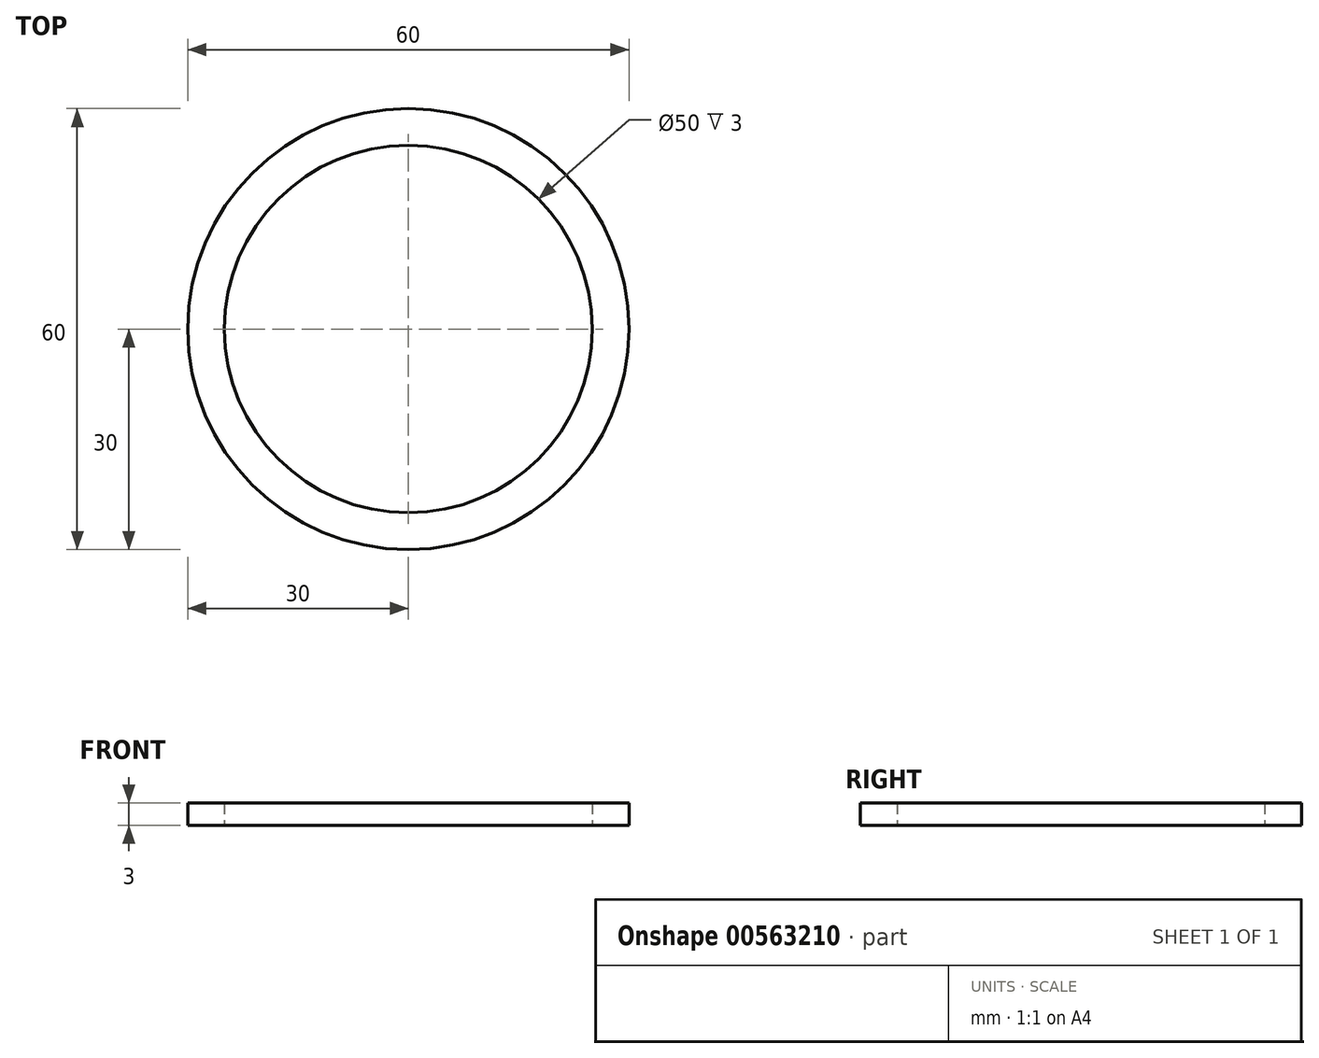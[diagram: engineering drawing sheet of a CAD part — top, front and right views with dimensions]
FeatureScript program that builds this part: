
annotation { "Feature Type Name" : "Feature", "Feature Type Description" : "" }
export const myFeature = defineFeature(function(context is Context, id is Id, definition is map)
    precondition{}
    {
        {
            var Q0;
            Q0=qCreatedBy(makeId("Top.planeOp"),FACE);
            var sketch = newSketch(context, id + "F0", { "sketchPlane" : qUnion([Q0])});
            skCircle(sketch, "E0", {"center": v(0, 0) * mm, "radius": 30 * mm});
            skCircle(sketch, "E1", {"center": v(0, 0) * mm, "radius": 25 * mm});
            skSolve(sketch);
        }
        {
            var Q0;
            Q0=qSketchRegion(id+"F0",true);
            extrude(context, id + "F1", {"entities" : qUnion([Q0]), "endBound" : BoundingType.SYMMETRIC, "depth" : 3 * mm, "offsetDistance" : 25 * mm});
        }
    });
